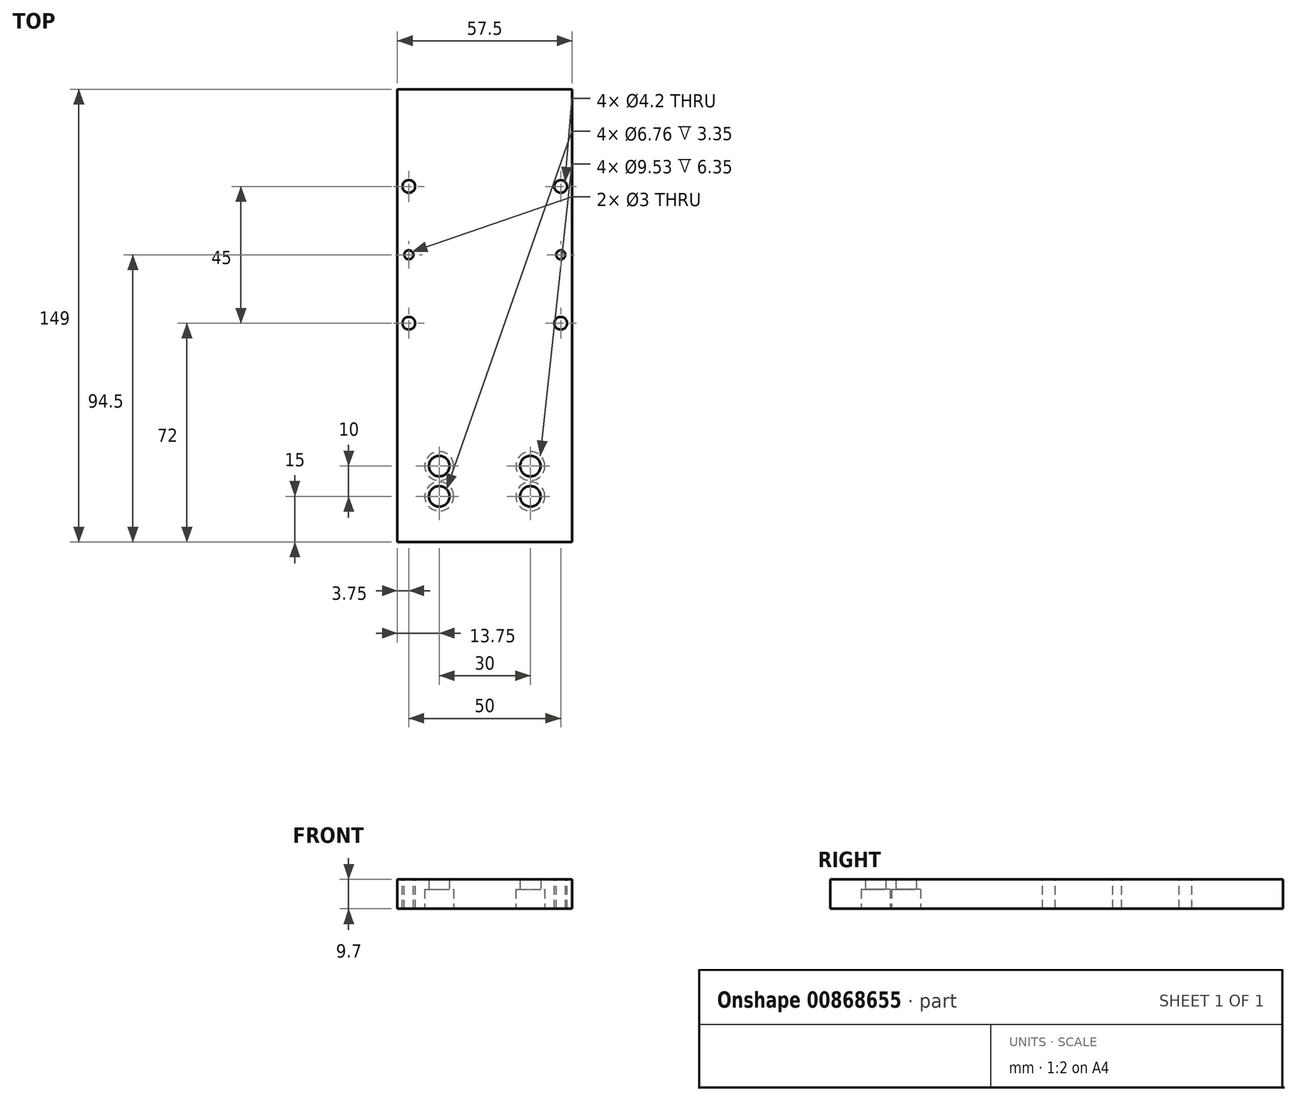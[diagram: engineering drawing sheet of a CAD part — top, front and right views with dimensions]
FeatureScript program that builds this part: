
annotation { "Feature Type Name" : "Feature", "Feature Type Description" : "" }
export const myFeature = defineFeature(function(context is Context, id is Id, definition is map)
    precondition{}
    {
        {
            var Q0;
            Q0=qCreatedBy(makeId("Top.planeOp"),FACE);
            var sketch = newSketch(context, id + "F0", { "sketchPlane" : qUnion([Q0])});
            skLineSegment(sketch, "E0.bottom", {"start": v(28.75, -74.5) * mm, "end": v(-28.75, -74.5) * mm});
            skLineSegment(sketch, "E0.top", {"start": v(28.75, 74.5) * mm, "end": v(-28.75, 74.5) * mm});
            skLineSegment(sketch, "E0.left", {"start": v(28.75, -74.5) * mm, "end": v(28.75, 74.5) * mm});
            skLineSegment(sketch, "E0.right", {"start": v(-28.75, -74.5) * mm, "end": v(-28.75, 74.5) * mm});
            skPoint(sketch, "E0.middle", {"position": v(0, 0) * mm});
            skLineSegment(sketch, "E1", {"start": v(0, 74.5) * mm, "end": v(0, -74.5) * mm, "construction": true});
            skLineSegment(sketch, "E2", {"start": v(-28.75, 20) * mm, "end": v(28.75, 20) * mm, "construction": true});
            skLineSegment(sketch, "E3", {"start": v(-28.75, -34.5) * mm, "end": v(28.75, -34.5) * mm, "construction": true});
            skLineSegment(sketch, "E4", {"start": v(-28.75, -49.5) * mm, "end": v(28.75, -49.5) * mm, "construction": true});
            skLineSegment(sketch, "E5", {"start": v(-28.75, -59.5) * mm, "end": v(28.75, -59.5) * mm, "construction": true});
            skLineSegment(sketch, "E6", {"start": v(-15, -34.5) * mm, "end": v(-15, -74.5) * mm, "construction": true});
            skLineSegment(sketch, "E7", {"start": v(15, -34.5) * mm, "end": v(15, -74.5) * mm, "construction": true});
            skLineSegment(sketch, "E8", {"start": v(-25, 74.5) * mm, "end": v(-25, -34.5) * mm, "construction": true});
            skLineSegment(sketch, "E9", {"start": v(25, 74.5) * mm, "end": v(25, -34.5) * mm, "construction": true});
            skLineSegment(sketch, "E10", {"start": v(-28.75, 42.5) * mm, "end": v(28.75, 42.5) * mm, "construction": true});
            skLineSegment(sketch, "E11", {"start": v(-28.75, -2.5) * mm, "end": v(28.75, -2.5) * mm, "construction": true});
            skPoint(sketch, "E12", {"position": v(-25, 20) * mm});
            skPoint(sketch, "E13", {"position": v(-25, 42.5) * mm});
            skPoint(sketch, "E14", {"position": v(-25, -2.5) * mm});
            skPoint(sketch, "E15", {"position": v(25, 20) * mm});
            skPoint(sketch, "E16", {"position": v(25, 42.5) * mm});
            skPoint(sketch, "E17", {"position": v(25, -2.5) * mm});
            skSolve(sketch);
        }
        {
            var Q0;
            Q0=makeQuery(id+"F0.imprint","IMPRINT",FACE,{"disambiguationData":[TD([[makeQuery(id+"F0.imprint","IMPRINT",EDGE,{"derivedFrom":sQuery(id+"F0.wireOp",EDGE,"E0.bottom")}),-1.0]])]});
            extrude(context, id + "F1", {"entities" : qUnion([Q0]), "depth" : -9.7 * mm, "offsetDistance" : 25 * mm});
        }
        {
            var Q0;
            Q0=sQuery(id+"F0.wireOp",VERTEX,"E13");
            var Q1;
            Q1=sQuery(id+"F0.wireOp",VERTEX,"E16");
            var Q2;
            Q2=sQuery(id+"F0.wireOp",VERTEX,"E14");
            var Q3;
            Q3=sQuery(id+"F0.wireOp",VERTEX,"E17");
            var Q4;
            Q4=makeQuery(id+"F1.opExtrude","SWEPT_BODY",BODY,{"disambiguationData":[OSD([sQuery(id+"F0.wireOp",EDGE,"E0.bottom"),sQuery(id+"F0.wireOp",EDGE,"E0.top"),sQuery(id+"F0.wireOp",EDGE,"E0.left"),sQuery(id+"F0.wireOp",EDGE,"E0.right")])]});
            hole(context, id + "F2", {"style" : HoleStyle.SIMPLE, "endStyle" : HoleEndStyle.THROUGH, "standardTappedOrClearance" : lookupTablePath({ "fit" : "Close", "standard" : "ISO", "size" : "M4", "type" : "Clearance" }), "standardBlindInLast" : lookupTablePath({ "fit" : "Close", "standard" : "ISO", "size" : "M4", "type" : "Clearance" }), "holeDiameter" : 4.2 * mm, "majorDiameter" : 5 * mm, "isTappedThrough" : true, "tappedDepth" : 19 * mm, "tapClearance" : 3, "locations" : qUnion([Q0, Q1, Q2, Q3]), "scope" : qUnion([Q4])});
        }
        {
            var Q0;
            Q0=sQuery(id+"F0.wireOp",VERTEX,"E12");
            var Q1;
            Q1=sQuery(id+"F0.wireOp",VERTEX,"E15");
            var Q2;
            Q2=makeQuery(id+"F1.opExtrude","SWEPT_BODY",BODY,{"disambiguationData":[OSD([sQuery(id+"F0.wireOp",EDGE,"E0.bottom"),sQuery(id+"F0.wireOp",EDGE,"E0.top"),sQuery(id+"F0.wireOp",EDGE,"E0.left"),sQuery(id+"F0.wireOp",EDGE,"E0.right")])]});
            hole(context, id + "F3", {"style" : HoleStyle.SIMPLE, "endStyle" : HoleEndStyle.THROUGH, "holeDiameter" : 3 * mm, "majorDiameter" : 5 * mm, "isTappedThrough" : true, "tappedDepth" : 19 * mm, "tapClearance" : 3, "locations" : qUnion([Q0, Q1]), "scope" : qUnion([Q2])});
        }
        {
            var Q0;
            Q0=makeQuery(id+"F1.opExtrude","CAP_FACE",FACE,{"disambiguationData":[OSD([sQuery(id+"F0.wireOp",EDGE,"E0.bottom"),sQuery(id+"F0.wireOp",EDGE,"E0.top"),sQuery(id+"F0.wireOp",EDGE,"E0.left"),sQuery(id+"F0.wireOp",EDGE,"E0.right")])],"isStart":false});
            var sketch = newSketch(context, id + "F4", { "sketchPlane" : qUnion([Q0])});
            skLineSegment(sketch, "E18", {"start": v(28.75, 34.5) * mm, "end": v(-28.75, 34.5) * mm, "construction": true});
            skLineSegment(sketch, "E19", {"start": v(28.75, 49.5) * mm, "end": v(-28.75, 49.5) * mm, "construction": true});
            skLineSegment(sketch, "E20", {"start": v(28.75, 59.5) * mm, "end": v(-28.75, 59.5) * mm, "construction": true});
            skLineSegment(sketch, "E21", {"start": v(-15, 34.5) * mm, "end": v(-15, 74.5) * mm, "construction": true});
            skLineSegment(sketch, "E22", {"start": v(15, 34.5) * mm, "end": v(15, 74.5) * mm, "construction": true});
            skLineSegment(sketch, "E23", {"start": v(0, 74.5) * mm, "end": v(0, 34.5) * mm, "construction": true});
            skPoint(sketch, "E24", {"position": v(-15, 49.5) * mm});
            skPoint(sketch, "E25", {"position": v(-15, 59.5) * mm});
            skPoint(sketch, "E26", {"position": v(15, 59.5) * mm});
            skPoint(sketch, "E27", {"position": v(15, 49.5) * mm});
            skSolve(sketch);
        }
        {
            var Q0;
            Q0=sQuery(id+"F4.wireOp",VERTEX,"E24");
            var Q1;
            Q1=sQuery(id+"F4.wireOp",VERTEX,"E27");
            var Q2;
            Q2=makeQuery(id+"F1.opExtrude","SWEPT_BODY",BODY,{"disambiguationData":[OSD([sQuery(id+"F0.wireOp",EDGE,"E0.bottom"),sQuery(id+"F0.wireOp",EDGE,"E0.top"),sQuery(id+"F0.wireOp",EDGE,"E0.left"),sQuery(id+"F0.wireOp",EDGE,"E0.right")])]});
            hole(context, id + "F5", {"style" : HoleStyle.C_BORE, "endStyle" : HoleEndStyle.BLIND, "holeDiameter" : 6.76 * mm, "cBoreDiameter" : 9.52 * mm, "cBoreDepth" : 6.35 * mm, "majorDiameter" : 5 * mm, "holeDepth" : 20 * mm, "isTappedThrough" : true, "tappedDepth" : 19 * mm, "tapClearance" : 3, "locations" : qUnion([Q0, Q1]), "scope" : qUnion([Q2])});
        }
        {
            var Q0;
            Q0=sQuery(id+"F4.wireOp",VERTEX,"E25");
            var Q1;
            Q1=sQuery(id+"F4.wireOp",VERTEX,"E26");
            var Q2;
            Q2=makeQuery(id+"F1.opExtrude","SWEPT_BODY",BODY,{"disambiguationData":[OSD([sQuery(id+"F0.wireOp",EDGE,"E0.bottom"),sQuery(id+"F0.wireOp",EDGE,"E0.top"),sQuery(id+"F0.wireOp",EDGE,"E0.left"),sQuery(id+"F0.wireOp",EDGE,"E0.right")])]});
            hole(context, id + "F6", {"style" : HoleStyle.C_BORE, "endStyle" : HoleEndStyle.BLIND, "holeDiameter" : 6.76 * mm, "cBoreDiameter" : 9.52 * mm, "cBoreDepth" : 6.35 * mm, "majorDiameter" : 5 * mm, "holeDepth" : 20 * mm, "isTappedThrough" : true, "tappedDepth" : 19 * mm, "tapClearance" : 3, "locations" : qUnion([Q0, Q1]), "scope" : qUnion([Q2])});
        }
    });
